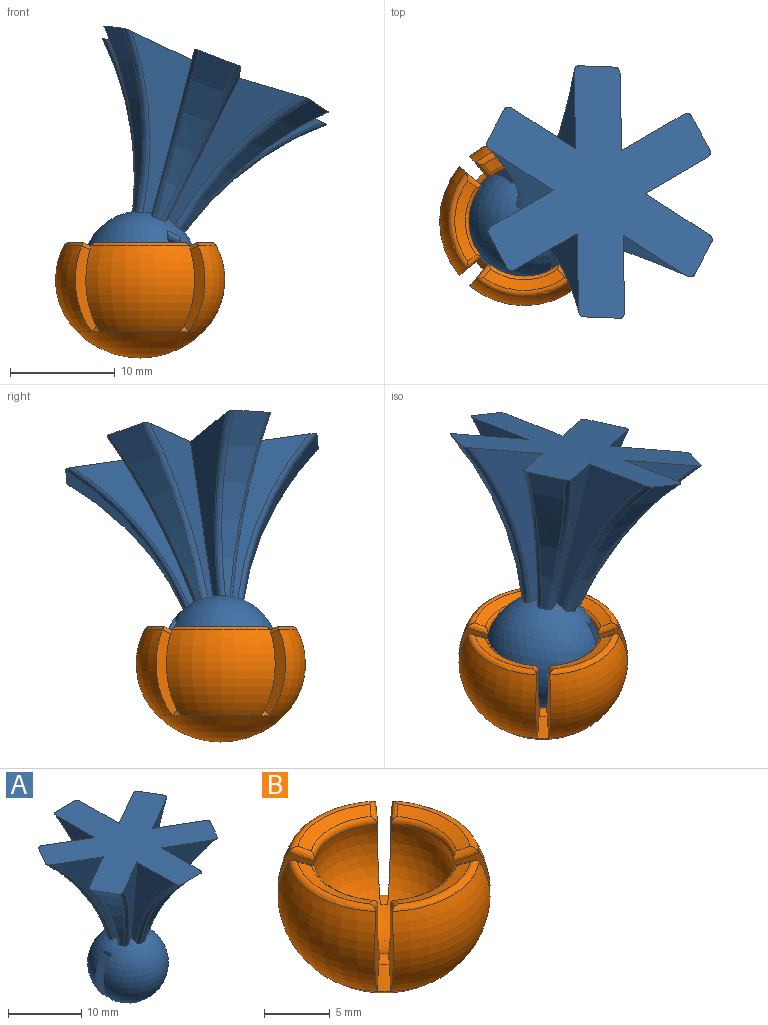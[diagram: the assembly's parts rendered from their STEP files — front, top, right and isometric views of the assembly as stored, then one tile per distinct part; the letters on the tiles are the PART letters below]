
ASSEMBLY  parts=2 mates=1
PART A: 37 faces, bbox 23.1x24.3x25.9 mm
  f0: cylinder r=30.17mm len=15.27mm, axis (-1,0,0), area 39mm2, adj f1,f2,f18,f31
  f1: bspline ~15.6x9.79mm, area 13.7mm2, adj f0,f18,f20,f31
  f2: bspline ~15.6x9.79mm, area 13.7mm2, adj f0,f18,f19,f31
  f3: cylinder r=30.17mm len=15.27mm, axis (-0.5,0.87,0), area 39mm2, adj f4,f5,f18,f31
  f4: bspline ~15.6x7.91mm, area 13.7mm2, adj f3,f18,f21,f31
  f5: bspline ~15.6x9.13mm, area 13.7mm2, adj f3,f18,f22,f31
  f6: cylinder r=30.17mm len=15.27mm, axis (0.5,0.87,0), area 39mm2, adj f7,f8,f18,f31
  f7: bspline ~15.6x9.13mm, area 13.7mm2, adj f6,f18,f23,f31
  f8: bspline ~15.6x7.91mm, area 13.7mm2, adj f6,f18,f24,f31
  f9: cylinder r=30.17mm len=15.27mm, axis (1,0,0), area 39mm2, adj f10,f11,f18,f31
  f10: bspline ~15.6x9.79mm, area 13.7mm2, adj f9,f18,f26,f31
  f11: bspline ~15.6x9.79mm, area 13.7mm2, adj f9,f18,f27,f31
  f12: cylinder r=30.17mm len=15.27mm, axis (0.5,-0.87,0), area 39mm2, adj f13,f14,f18,f31
  f13: bspline ~15.6x7.91mm, area 13.7mm2, adj f12,f18,f28,f31
  f14: bspline ~15.6x9.13mm, area 13.7mm2, adj f12,f18,f29,f31
  f15: cylinder r=30.17mm len=15.27mm, axis (-0.5,-0.87,0), area 39mm2, adj f16,f17,f18,f31
  f16: bspline ~15.6x9.13mm, area 13.7mm2, adj f15,f18,f30,f31
  f17: bspline ~15.6x7.91mm, area 13.7mm2, adj f15,f18,f25,f31
  f18: plane 24.2x22.94mm, normal (0,0,1), area 283.3mm2, adj f0,f1,f2,f3,f4,f5,f6,f7
  f19: plane 15.18x10.11mm, normal (-0.99,0,-0.1), area 47.9mm2, adj f2,f18,f21,f31
  f20: plane 15.18x10.11mm, normal (0.99,0,-0.1), area 47.9mm2, adj f1,f18,f25,f31
  f21: plane 15.18x8mm, normal (0.5,-0.86,-0.1), area 47.9mm2, adj f4,f18,f19,f31
  f22: plane 15.18x9.55mm, normal (-0.5,0.86,-0.1), area 47.9mm2, adj f5,f18,f23,f31
  f23: plane 15.18x9.55mm, normal (-0.5,-0.86,-0.1), area 47.9mm2, adj f7,f18,f22,f31
  f24: plane 15.18x8mm, normal (0.5,0.86,-0.1), area 47.9mm2, adj f8,f18,f26,f31
  f25: plane 15.18x8mm, normal (-0.5,-0.86,-0.1), area 47.9mm2, adj f17,f18,f20,f31
  f26: plane 15.18x10.11mm, normal (-0.99,0,-0.1), area 47.9mm2, adj f10,f18,f24,f31
  f27: plane 15.18x10.11mm, normal (0.99,0,-0.1), area 47.9mm2, adj f11,f18,f28,f31
  f28: plane 15.18x8mm, normal (-0.5,0.86,-0.1), area 47.9mm2, adj f13,f18,f27,f31
  f29: plane 15.08x9.45mm, normal (0.5,-0.86,-0.1), area 47.9mm2, adj f14,f18,f30,f31
  f30: plane 15.08x9.45mm, normal (0.5,0.86,-0.1), area 47.9mm2, adj f16,f18,f29,f31
  f31: sphere r=5.5mm, area 321.3mm2, adj f0,f1,f2,f3,f4,f5,f6,f7
  f32: plane 7.14x1.5mm, normal (0,0,-1), area 10.6mm2, adj f33,f34,f35,f36
  f33: plane 10.9x9.3mm, normal (0,1,0), area 78.1mm2, adj f31,f32,f35,f36
  f34: plane 10.9x9.3mm, normal (0,-1,0), area 78.1mm2, adj f31,f32,f35,f36
  f35: torus R=3.57mm, axis (0,0,-1), area 1.8mm2, adj f31,f32,f33,f34
  f36: torus R=3.57mm, axis (0,0,-1), area 1.8mm2, adj f31,f32,f33,f34
PART B: 42 faces, bbox 25.5x25.5x14.6 mm
  f0: cone r=3.89mm half-angle=45deg, axis (0,0,-1), area 1.9mm2, adj f4,f24,f33,f38
  f1: cone r=3.89mm half-angle=45deg, axis (0,0,-1), area 1.9mm2, adj f4,f16,f25,f39
  f2: cone r=3.89mm half-angle=45deg, axis (0,0,-1), area 1.9mm2, adj f4,f8,f17,f40
  f3: sphere r=5.5mm, area 218.9mm2, adj f8,f9,f10,f11,f12,f16,f17,f18
  f4: sphere r=8.5mm, area 133mm2, adj f0,f1,f2,f5,f6,f14,f22,f30
  f5: cone r=3.89mm half-angle=45deg, axis (0,0,-1), area 1.9mm2, adj f4,f9,f32,f41
  f6: torus R=1.05mm, axis (0,0,1), area 94mm2, adj f4,f8,f9,f11,f12,f13
  f7: cone r=5.15mm half-angle=69.4deg, axis (0,0,1), area 8.3mm2, adj f10,f11,f12,f13
  f8: plane 8.21x3.69mm, normal (-0.64,-0.77,0), area 19.8mm2, adj f2,f3,f6,f11,f40
  f9: plane 8.21x3.69mm, normal (-0.64,0.77,0), area 19.8mm2, adj f3,f5,f6,f12,f41
  f10: torus R=5.77mm, axis (0,0,-1), area 5.2mm2, adj f3,f7,f11,f12
  f11: bspline ~5.52x4.85mm, area 1.3mm2, adj f3,f6,f7,f8,f10,f13
  f12: bspline ~9.4x8.1mm, area 1.3mm2, adj f3,f6,f7,f9,f10,f13
  f13: torus R=6.8mm, axis (0,0,-1), area 6.6mm2, adj f6,f7,f11,f12
  f14: torus R=1.05mm, axis (0,0,1), area 94mm2, adj f4,f16,f17,f19,f20,f21
  f15: cone r=5.15mm half-angle=69.4deg, axis (0,0,1), area 8.3mm2, adj f18,f19,f20,f21
  f16: plane 8.21x3.69mm, normal (-0.77,0.64,0), area 19.8mm2, adj f1,f3,f14,f19,f39
  f17: plane 8.21x3.69mm, normal (0.77,0.64,0), area 19.8mm2, adj f2,f3,f14,f20,f40
  f18: torus R=5.77mm, axis (0,0,-1), area 5.2mm2, adj f3,f15,f19,f20
  f19: bspline ~5.52x4.85mm, area 1.3mm2, adj f3,f14,f15,f16,f18,f21
  f20: bspline ~9.4x8.1mm, area 1.3mm2, adj f3,f14,f15,f17,f18,f21
  f21: torus R=6.8mm, axis (0,0,-1), area 6.6mm2, adj f14,f15,f19,f20
  f22: torus R=1.05mm, axis (0,0,1), area 94mm2, adj f4,f24,f25,f27,f28,f29
  f23: cone r=5.15mm half-angle=69.4deg, axis (0,0,1), area 8.3mm2, adj f26,f27,f28,f29
  f24: plane 8.21x3.69mm, normal (0.64,0.77,0), area 19.8mm2, adj f0,f3,f22,f27,f38
  f25: plane 8.21x3.69mm, normal (0.64,-0.77,0), area 19.8mm2, adj f1,f3,f22,f28,f39
  f26: torus R=5.77mm, axis (0,0,-1), area 5.2mm2, adj f3,f23,f27,f28
  f27: bspline ~5.52x4.85mm, area 1.3mm2, adj f3,f22,f23,f24,f26,f29
  f28: bspline ~9.4x8.1mm, area 1.3mm2, adj f3,f22,f23,f25,f26,f29
  f29: torus R=6.8mm, axis (0,0,-1), area 6.6mm2, adj f22,f23,f27,f28
  f30: torus R=1.05mm, axis (0,0,1), area 94mm2, adj f4,f32,f33,f35,f36,f37
  f31: cone r=5.15mm half-angle=69.4deg, axis (0,0,1), area 8.3mm2, adj f34,f35,f36,f37
  f32: plane 8.21x3.69mm, normal (0.77,-0.64,0), area 19.8mm2, adj f3,f5,f30,f35,f41
  f33: plane 8.21x3.69mm, normal (-0.77,-0.64,0), area 19.8mm2, adj f0,f3,f30,f36,f38
  f34: torus R=5.77mm, axis (0,0,-1), area 5.2mm2, adj f3,f31,f35,f36
  f35: bspline ~5.52x4.85mm, area 1.3mm2, adj f3,f30,f31,f32,f34,f37
  f36: bspline ~9.4x8.1mm, area 1.3mm2, adj f3,f30,f31,f33,f34,f37
  f37: torus R=6.8mm, axis (0,0,-1), area 6.6mm2, adj f30,f31,f35,f36
  f38: torus R=3.83mm, axis (0,0,1), area 1mm2, adj f0,f3,f24,f33
  f39: torus R=3.83mm, axis (0,0,1), area 1mm2, adj f1,f3,f16,f25
  f40: torus R=3.83mm, axis (0,0,1), area 1mm2, adj f2,f3,f8,f17
  f41: torus R=3.83mm, axis (0,0,1), area 1mm2, adj f3,f5,f9,f32
PLACE A rot(axis=(-0.29,0.23,-0.93),64.2deg) t=(0,0,0)mm
PLACE B at identity
MATE ball A.f35 <-> B.f0  axis (0.36,0.14,0.92) through (0,0,0)mm
